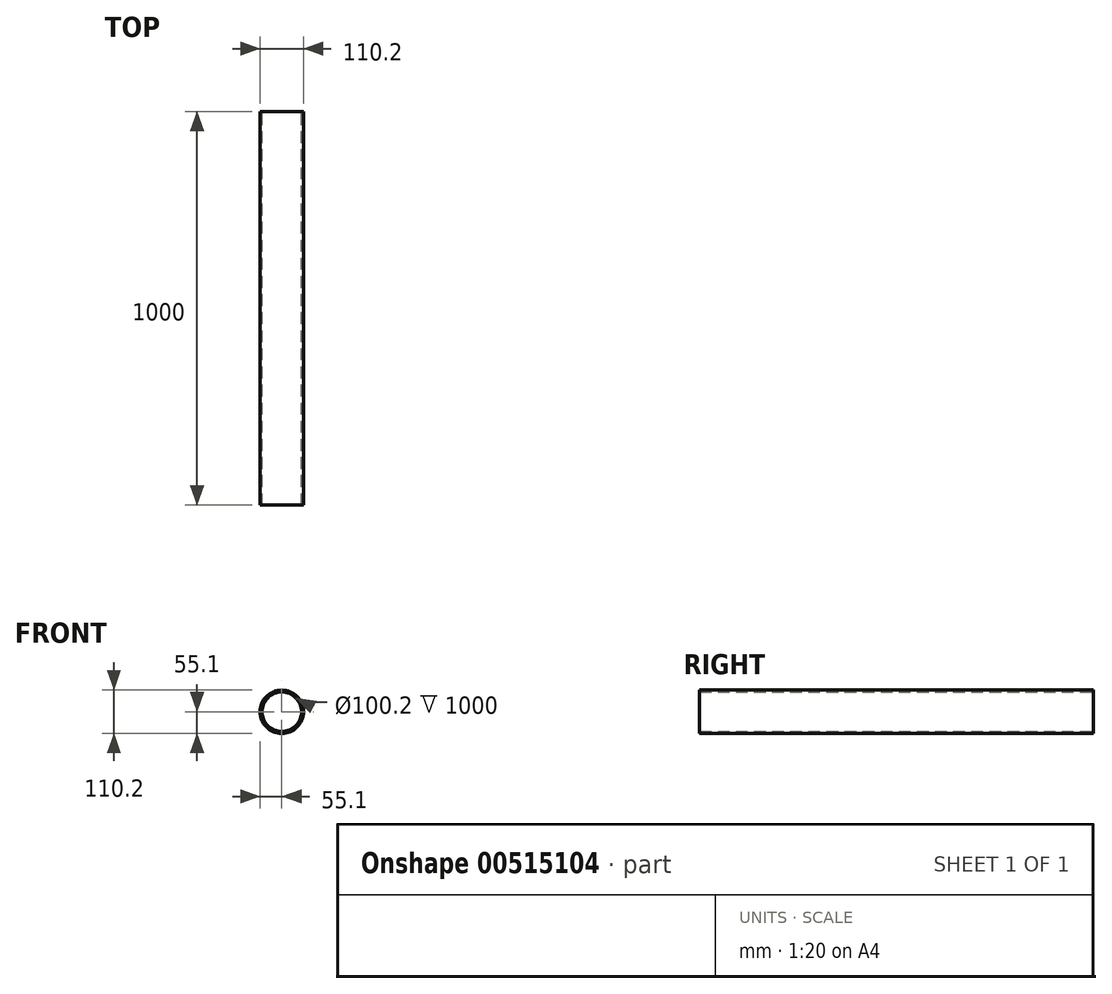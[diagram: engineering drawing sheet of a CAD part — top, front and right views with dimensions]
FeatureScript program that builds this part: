
annotation { "Feature Type Name" : "Feature", "Feature Type Description" : "" }
export const myFeature = defineFeature(function(context is Context, id is Id, definition is map)
    precondition{}
    {
        {
            var Q0;
            Q0=qCreatedBy(makeId("Front.planeOp"),FACE);
            var sketch = newSketch(context, id + "F0", { "sketchPlane" : qUnion([Q0])});
            skCircle(sketch, "E0", {"center": v(0, 0) * mm, "radius": 55.1 * mm});
            skCircle(sketch, "E1.0", {"center": v(0, 0) * mm, "radius": 50.1 * mm});
            skSolve(sketch);
        }
        {
            var Q0;
            Q0=makeQuery(id+"F0.imprint","IMPRINT",FACE,{"disambiguationData":[TD([[makeQuery(id+"F0.imprint","IMPRINT",EDGE,{"derivedFrom":sQuery(id+"F0.wireOp",EDGE,"E0")}),1.0]])]});
            extrude(context, id + "F1", {"entities" : qUnion([Q0]), "depth" : 1000 * mm, "offsetDistance" : 25 * mm});
        }
    });
